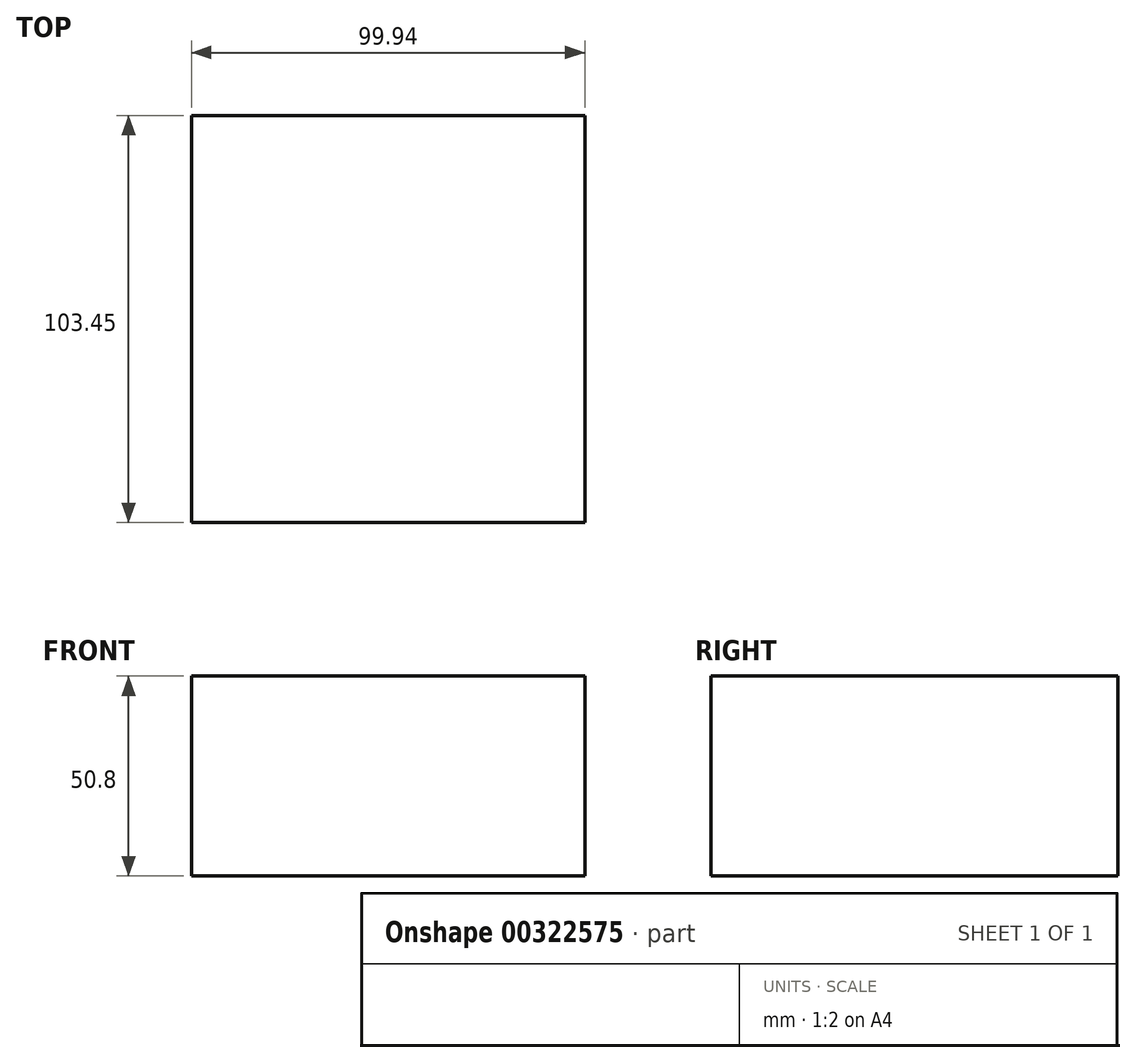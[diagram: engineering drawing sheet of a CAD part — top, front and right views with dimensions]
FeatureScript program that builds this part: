
annotation { "Feature Type Name" : "Feature", "Feature Type Description" : "" }
export const myFeature = defineFeature(function(context is Context, id is Id, definition is map)
    precondition{}
    {
        {
            var Q0;
            Q0=qCreatedBy(makeId("Top.planeOp"),FACE);
            var sketch = newSketch(context, id + "F0", { "sketchPlane" : qUnion([Q0])});
            skLineSegment(sketch, "E0.bottom", {"start": v(-49.3, -53.3) * mm, "end": v(50.63, -53.3) * mm});
            skLineSegment(sketch, "E0.top", {"start": v(-49.3, 50.16) * mm, "end": v(50.63, 50.16) * mm});
            skLineSegment(sketch, "E0.left", {"start": v(-49.3, -53.3) * mm, "end": v(-49.3, 50.16) * mm});
            skLineSegment(sketch, "E0.right", {"start": v(50.63, -53.3) * mm, "end": v(50.63, 50.16) * mm});
            skSolve(sketch);
        }
        {
            var Q0;
            Q0=makeQuery(id+"F0.imprint","IMPRINT",FACE,{"disambiguationData":[TD([[makeQuery(id+"F0.imprint","IMPRINT",EDGE,{"derivedFrom":sQuery(id+"F0.wireOp",EDGE,"E0.bottom")}),1.0]])]});
            extrude(context, id + "F1", {"entities" : qUnion([Q0]), "depth" : 50.8 * mm, "offsetDistance" : 25.4 * mm});
        }
    });
